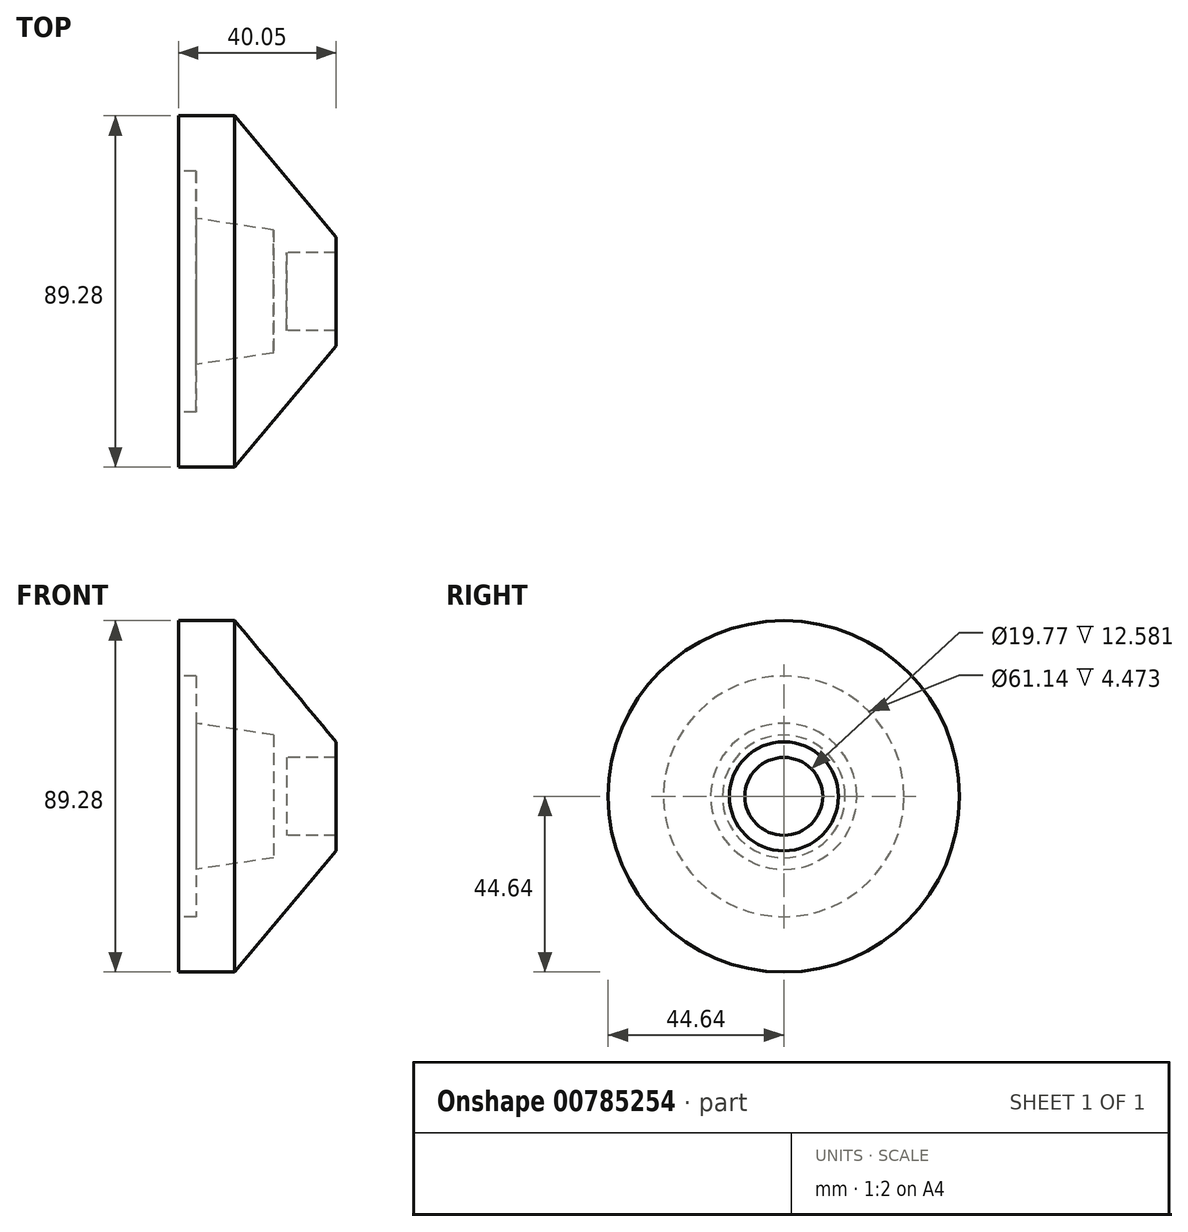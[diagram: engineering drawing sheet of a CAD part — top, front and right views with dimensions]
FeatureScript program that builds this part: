
annotation { "Feature Type Name" : "Feature", "Feature Type Description" : "" }
export const myFeature = defineFeature(function(context is Context, id is Id, definition is map)
    precondition{}
    {
        {
            var Q0;
            Q0=qCreatedBy(makeId("Front.planeOp"),FACE);
            var sketch = newSketch(context, id + "F0", { "sketchPlane" : qUnion([Q0])});
            skLineSegment(sketch, "E0", {"start": v(0, 44.64) * mm, "end": v(0, 30.57) * mm});
            skLineSegment(sketch, "E1", {"start": v(0, 30.57) * mm, "end": v(4.47, 30.57) * mm});
            skLineSegment(sketch, "E2", {"start": v(4.47, 30.57) * mm, "end": v(4.47, 18.57) * mm});
            skLineSegment(sketch, "E3", {"start": v(4.47, 18.57) * mm, "end": v(24.17, 15.6) * mm});
            skLineSegment(sketch, "E4", {"start": v(24.17, 15.6) * mm, "end": v(24.17, 0) * mm});
            skLineSegment(sketch, "E5", {"start": v(24.17, 0) * mm, "end": v(27.47, 0) * mm});
            skLineSegment(sketch, "E6", {"start": v(27.47, 0) * mm, "end": v(27.47, 9.88) * mm});
            skLineSegment(sketch, "E7", {"start": v(27.47, 9.88) * mm, "end": v(40.05, 9.88) * mm});
            skLineSegment(sketch, "E8", {"start": v(40.05, 9.88) * mm, "end": v(40.05, 13.85) * mm});
            skLineSegment(sketch, "E9", {"start": v(40.05, 13.85) * mm, "end": v(14.32, 44.64) * mm});
            skPoint(sketch, "E9.endSnap0", {"position": v(14.32, 17.08) * mm});
            skLineSegment(sketch, "E10", {"start": v(14.32, 44.64) * mm, "end": v(0, 44.64) * mm});
            skLineSegment(sketch, "E11", {"start": v(-25.98, 0) * mm, "end": v(46.84, 0) * mm});
            skSolve(sketch);
        }
        {
            var Q0;
            Q0=makeQuery(id+"F0.imprint","IMPRINT",FACE,{"disambiguationData":[TD([[makeQuery(id+"F0.imprint","IMPRINT",EDGE,{"derivedFrom":sQuery(id+"F0.wireOp",EDGE,"E0")}),1.0]])]});
            var Q1;
            Q1=sQuery(id+"F0.wireOp",EDGE,"E11");
            revolve(context, id + "F1", {"surfaceOperationType" : NewSurfaceOperationType.NEW, "entities" : qUnion([Q0]), "axis" : qUnion([Q1]), "revolveType" : RevolveType.FULL});
        }
    });
